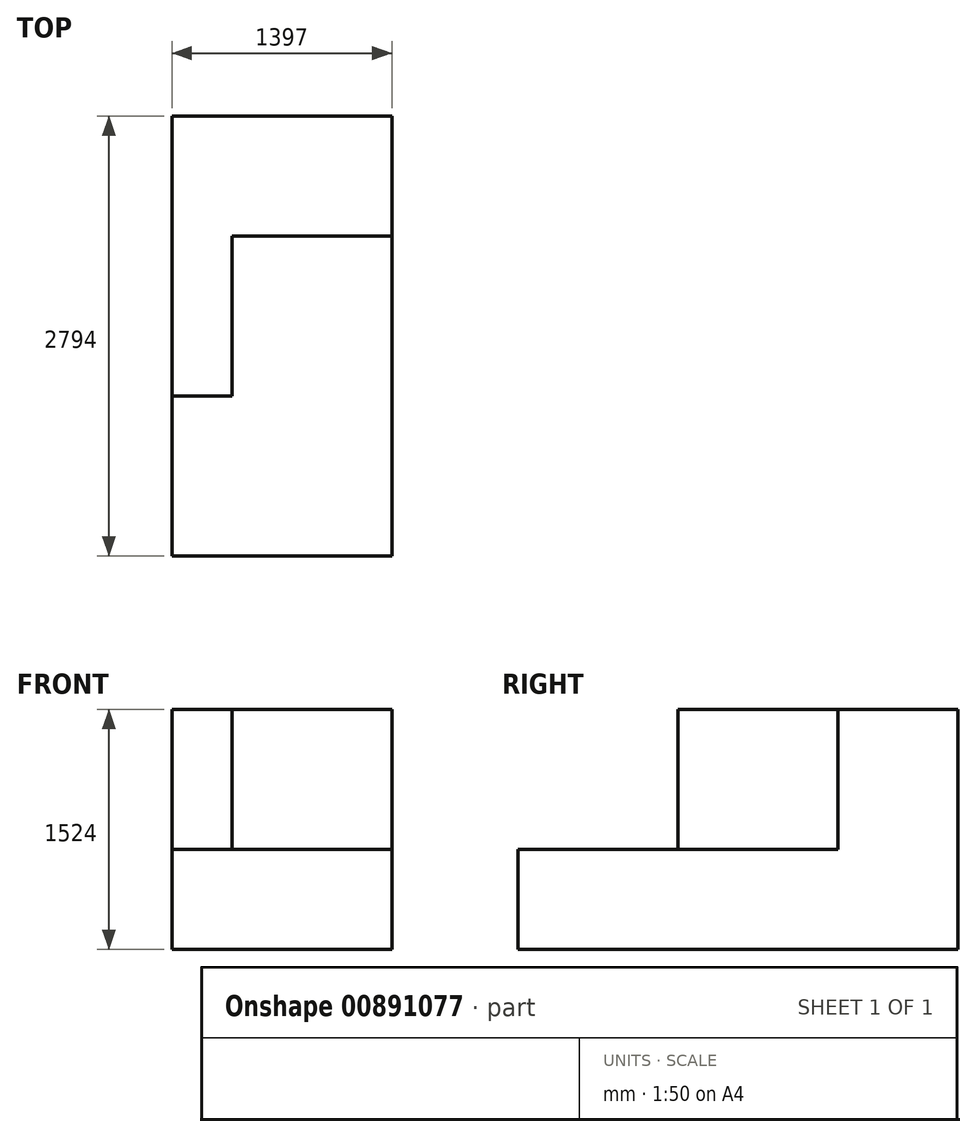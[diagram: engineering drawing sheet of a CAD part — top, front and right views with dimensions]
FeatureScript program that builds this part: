
annotation { "Feature Type Name" : "Feature", "Feature Type Description" : "" }
export const myFeature = defineFeature(function(context is Context, id is Id, definition is map)
    precondition{}
    {
        {
            var Q0;
            Q0=qCreatedBy(makeId("Right.planeOp"),FACE);
            var sketch = newSketch(context, id + "F0", { "sketchPlane" : qUnion([Q0])});
            skLineSegment(sketch, "E0.bottom", {"start": v(-2688.3, 1478.14) * mm, "end": v(105.7, 1478.14) * mm});
            skLineSegment(sketch, "E0.top", {"start": v(-2688.3, -45.86) * mm, "end": v(105.7, -45.86) * mm});
            skLineSegment(sketch, "E0.left", {"start": v(-2688.3, 1478.14) * mm, "end": v(-2688.3, -45.86) * mm});
            skLineSegment(sketch, "E0.right", {"start": v(105.7, 1478.14) * mm, "end": v(105.7, -45.86) * mm});
            skSolve(sketch);
        }
        {
            var Q0;
            Q0=makeQuery(id+"F0.imprint","IMPRINT",FACE,{"disambiguationData":[TD([[makeQuery(id+"F0.imprint","IMPRINT",EDGE,{"derivedFrom":sQuery(id+"F0.wireOp",EDGE,"E0.bottom")}),-1.0]])]});
            var sketch = newSketch(context, id + "F1", { "sketchPlane" : qUnion([Q0])});
            skSolve(sketch);
        }
        {
            var Q0;
            Q0 = qSketchRegion(id + "F1", true);
            var Q1;
            Q1=makeQuery(id+"F1.imprint","IMPRINT",FACE,{"disambiguationData":[TD([[makeQuery(id+"F1.imprint","IMPRINT",EDGE,{"derivedFrom":makeQuery(id+"F0.imprint","IMPRINT",EDGE,{"derivedFrom":sQuery(id+"F0.wireOp",EDGE,"E0.bottom")})}),-1.0]])]});
            extrude(context, id + "F2", {"entities" : qUnion([Q0, Q1]), "depth" : 1397 * mm, "offsetDistance" : 25.4 * mm});
        }
        {
            var Q0;
            Q0=makeQuery(id+"F2.opExtrude","SWEPT_FACE",FACE,{"disambiguationData":[OSD([sQuery(id+"F0.wireOp",EDGE,"E0.left")])]});
            var sketch = newSketch(context, id + "F3", { "sketchPlane" : qUnion([Q0])});
            skLineSegment(sketch, "E1", {"start": v(0, -45.86) * mm, "end": v(381, -45.86) * mm});
            skLineSegment(sketch, "E2", {"start": v(381, -45.86) * mm, "end": v(381, 589.14) * mm});
            skLineSegment(sketch, "E3", {"start": v(381, 589.14) * mm, "end": v(0, 589.14) * mm});
            skLineSegment(sketch, "E4", {"start": v(0, 589.14) * mm, "end": v(0, 1478.14) * mm});
            skLineSegment(sketch, "E5", {"start": v(0, 1478.14) * mm, "end": v(381, 1478.14) * mm});
            skLineSegment(sketch, "E6", {"start": v(381, 1478.14) * mm, "end": v(381, 589.14) * mm});
            skLineSegment(sketch, "E7", {"start": v(1397, 589.14) * mm, "end": v(381, 589.14) * mm});
            skSolve(sketch);
        }
        {
            var Q0;
            Q0=makeQuery(id+"F3.imprint","IMPRINT",FACE,{"disambiguationData":[TD([[makeQuery(id+"F3.imprint","IMPRINT",EDGE,{"derivedFrom":sQuery(id+"F3.wireOp",EDGE,"E3")}),-1.0]])]});
            extrude(context, id + "F4", {"entities" : qUnion([Q0]), "operationType" : NewBodyOperationType.REMOVE, "oppositeDirection" : true, "depth" : 1016 * mm, "offsetDistance" : 25.4 * mm});
        }
        {
            var Q0;
            Q0=makeQuery(id+"F2.opExtrude","SWEPT_FACE",FACE,{"disambiguationData":[OSD([sQuery(id+"F0.wireOp",EDGE,"E0.left")])]});
            var sketch = newSketch(context, id + "F5", { "sketchPlane" : qUnion([Q0])});
            skLineSegment(sketch, "E8", {"start": v(381, 589.14) * mm, "end": v(1397, 589.14) * mm});
            skSolve(sketch);
        }
        {
            var Q0;
            {var subQ0=sQuery(id+"F5.wireOp",EDGE,"E8");Q0=makeQuery(id+"F5.imprint","IMPRINT",FACE,{"disambiguationData":[TD([[makeQuery(id+"F5.imprint","IMPRINT",EDGE,{"derivedFrom":subQ0}),1.0]])]});}
            extrude(context, id + "F6", {"entities" : qUnion([Q0]), "operationType" : NewBodyOperationType.REMOVE, "depth" : 2.54 * mm, "offsetDistance" : 25.4 * mm});
        }
        {
            var Q0;
            Q0=makeQuery(id+"F2.opExtrude","SWEPT_FACE",FACE,{"disambiguationData":[OSD([sQuery(id+"F0.wireOp",EDGE,"E0.left")])]});
            var sketch = newSketch(context, id + "F7", { "sketchPlane" : qUnion([Q0])});
            skLineSegment(sketch, "E9", {"start": v(381, 589.14) * mm, "end": v(1397, 589.14) * mm});
            skSolve(sketch);
        }
        {
            var Q0;
            {var subQ0=sQuery(id+"F7.wireOp",EDGE,"E9");Q0=makeQuery(id+"F7.imprint","IMPRINT",FACE,{"disambiguationData":[TD([[makeQuery(id+"F7.imprint","IMPRINT",EDGE,{"derivedFrom":subQ0}),1.0]])]});}
            extrude(context, id + "F8", {"entities" : qUnion([Q0]), "operationType" : NewBodyOperationType.REMOVE, "oppositeDirection" : true, "depth" : 2032 * mm, "offsetDistance" : 25.4 * mm});
        }
    });
